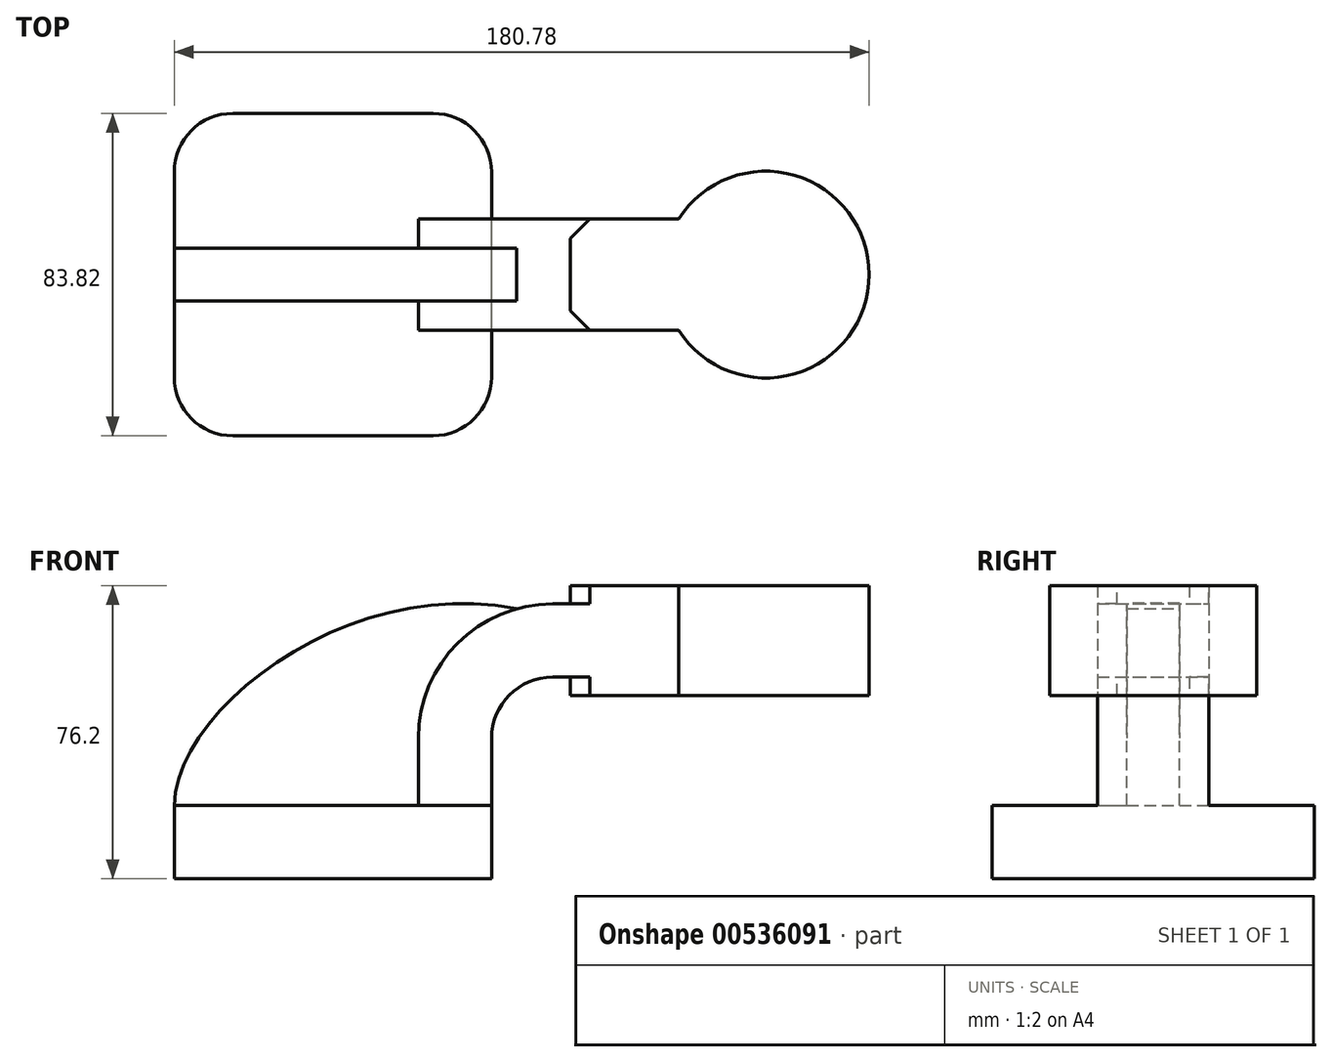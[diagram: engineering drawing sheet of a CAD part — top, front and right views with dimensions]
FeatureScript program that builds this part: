
annotation { "Feature Type Name" : "Feature", "Feature Type Description" : "" }
export const myFeature = defineFeature(function(context is Context, id is Id, definition is map)
    precondition{}
    {
        {
            var Q0;
            Q0=qCreatedBy(makeId("Front.planeOp"),FACE);
            var sketch = newSketch(context, id + "F0", { "sketchPlane" : qUnion([Q0])});
            skLineSegment(sketch, "E0.bottom", {"start": v(-41.28, 9.52) * mm, "end": v(41.27, 9.53) * mm});
            skLineSegment(sketch, "E0.top", {"start": v(-41.28, -9.53) * mm, "end": v(41.28, -9.53) * mm});
            skLineSegment(sketch, "E0.left", {"start": v(-41.28, 9.52) * mm, "end": v(-41.28, -9.53) * mm});
            skLineSegment(sketch, "E0.right", {"start": v(41.27, 9.53) * mm, "end": v(41.28, -9.52) * mm});
            skPoint(sketch, "E0.middle", {"position": v(0, 0) * mm});
            skLineSegment(sketch, "E1.bottom", {"start": v(61.81, 38.1) * mm, "end": v(112.61, 38.1) * mm});
            skLineSegment(sketch, "E1.top", {"start": v(61.81, 66.68) * mm, "end": v(112.61, 66.68) * mm});
            skLineSegment(sketch, "E1.left", {"start": v(61.81, 38.1) * mm, "end": v(61.81, 66.68) * mm});
            skLineSegment(sketch, "E1.right", {"start": v(112.61, 38.1) * mm, "end": v(112.61, 66.68) * mm});
            skPoint(sketch, "E1.middle", {"position": v(87.21, 52.39) * mm});
            skLineSegment(sketch, "E2", {"start": v(41.27, 9.53) * mm, "end": v(41.27, 27) * mm});
            skArc(sketch, "E3", {"start": v(41.27, 27) * mm, "mid": v(45.92, 38.23) * mm, "end": v(57.15, 42.88) * mm});
            skLineSegment(sketch, "E4", {"start": v(57.15, 42.88) * mm, "end": v(85.72, 42.88) * mm});
            skLineSegment(sketch, "E5.0", {"start": v(57.15, 61.93) * mm, "end": v(85.72, 61.93) * mm});
            skArc(sketch, "E5.1", {"start": v(22.22, 27) * mm, "mid": v(32.45, 51.7) * mm, "end": v(57.15, 61.93) * mm});
            skLineSegment(sketch, "E5.2", {"start": v(22.22, 9.53) * mm, "end": v(22.22, 27) * mm});
            skLineSegment(sketch, "E6", {"start": v(85.72, 42.88) * mm, "end": v(85.72, 66.68) * mm});
            skPoint(sketch, "E6.endSnap0", {"position": v(87.21, 66.68) * mm});
            skLineSegment(sketch, "E7", {"start": v(85.72, 66.68) * mm, "end": v(85.72, 38.1) * mm});
            skPoint(sketch, "E7.endSnap0", {"position": v(87.21, 38.1) * mm});
            skFitSpline(sketch, "E8", {"points": [v(-41.28, 9.53) * mm, v(47.83, 60.66) * mm], "startDerivative": vector(2.6, 78.56) * mm, "endDerivative": vector(127.58, -26.35) * mm});
            skSolve(sketch);
        }
        {
            var Q0;
            Q0=makeQuery(id+"F0.imprint","IMPRINT",FACE,{"disambiguationData":[TD([[makeQuery(id+"F0.imprint","IMPRINT",EDGE,{"derivedFrom":sQuery(id+"F0.wireOp",EDGE,"E0.top")}),1.0]])]});
            extrude(context, id + "F1", {"entities" : qUnion([Q0]), "endBound" : BoundingType.SYMMETRIC, "depth" : 83.82 * mm, "offsetDistance" : 25.4 * mm});
        }
        {
            var Q0;
            {var subQ0=sQuery(id+"F0.wireOp",EDGE,"E4");var subQ1=sQuery(id+"F0.wireOp",EDGE,"E1.left");var subQ2=makeQuery(id+"F0.imprint","INTERSECT",VERTEX,{"derivedFrom":[subQ1,subQ0]});Q0=makeQuery(id+"F0.imprint","IMPRINT",FACE,{"disambiguationData":[TD([[makeQuery(id+"F0.imprint","IMPRINT",EDGE,{"disambiguationData":[TD([[subQ2,-1.0]])],"derivedFrom":subQ1}),-1.0]])]});}
            var Q1;
            {var subQ4=sQuery(id+"F0.wireOp",EDGE,"E1.right");Q1=makeQuery(id+"F0.imprint","IMPRINT",FACE,{"disambiguationData":[TD([[makeQuery(id+"F0.imprint","IMPRINT",EDGE,{"derivedFrom":subQ4}),1.0]])]});}
            var Q2;
            {var subQ0=sQuery(id+"F0.wireOp",EDGE,"E1.left");var subQ1=sQuery(id+"F0.wireOp",EDGE,"E1.top");var subQ2=makeQuery(id+"F0.imprint","INTERSECT",VERTEX,{"derivedFrom":[subQ1,subQ0]});Q2=makeQuery(id+"F0.imprint","IMPRINT",FACE,{"disambiguationData":[TD([[makeQuery(id+"F0.imprint","IMPRINT",EDGE,{"disambiguationData":[TD([[subQ2,-1.0]])],"derivedFrom":subQ1}),-1.0]])]});}
            var Q3;
            {var subQ0=sQuery(id+"F0.wireOp",EDGE,"E1.left");var subQ1=sQuery(id+"F0.wireOp",EDGE,"E1.bottom");var subQ2=makeQuery(id+"F0.imprint","INTERSECT",VERTEX,{"derivedFrom":[subQ1,subQ0]});Q3=makeQuery(id+"F0.imprint","IMPRINT",FACE,{"disambiguationData":[TD([[makeQuery(id+"F0.imprint","IMPRINT",EDGE,{"disambiguationData":[TD([[subQ2,-1.0]])],"derivedFrom":subQ1}),1.0]])]});}
            var Q4;
            {var subQ1=sQuery(id+"F0.wireOp",EDGE,"E2");Q4=makeQuery(id+"F0.imprint","IMPRINT",FACE,{"disambiguationData":[TD([[makeQuery(id+"F0.imprint","IMPRINT",EDGE,{"derivedFrom":subQ1}),1.0]])]});}
            extrude(context, id + "F2", {"entities" : qUnion([Q0, Q1, Q2, Q3, Q4]), "operationType" : NewBodyOperationType.ADD, "endBound" : BoundingType.SYMMETRIC, "depth" : 28.96 * mm, "offsetDistance" : 25.4 * mm});
        }
        {
            var Q0;
            {var subQ2=sQuery(id+"F0.wireOp",EDGE,"E5.2");Q0=makeQuery(id+"F0.imprint","IMPRINT",FACE,{"disambiguationData":[TD([[makeQuery(id+"F0.imprint","IMPRINT",EDGE,{"derivedFrom":subQ2}),1.0]])]});}
            extrude(context, id + "F3", {"entities" : qUnion([Q0]), "operationType" : NewBodyOperationType.ADD, "endBound" : BoundingType.SYMMETRIC, "depth" : 13.72 * mm, "offsetDistance" : 25.4 * mm});
        }
        {
            var Q0;
            {var subQ4=sQuery(id+"F0.wireOp",EDGE,"E1.right");Q0=makeQuery(id+"F0.imprint","IMPRINT",FACE,{"disambiguationData":[TD([[makeQuery(id+"F0.imprint","IMPRINT",EDGE,{"derivedFrom":subQ4}),1.0]])]});}
            var Q1;
            Q1=sQuery(id+"F0.wireOp",EDGE,"E1.right");
            revolve(context, id + "F4", {"operationType" : NewBodyOperationType.ADD, "entities" : qUnion([Q0]), "axis" : qUnion([Q1]), "revolveType" : RevolveType.FULL});
        }
        {
            var Q0;
            Q0=makeQuery(id+"F1.opExtrude","CAP_EDGE",EDGE,{"disambiguationData":[OSD([sQuery(id+"F0.wireOp",EDGE,"E0.left")])],"isStart":false});
            var Q1;
            Q1=makeQuery(id+"F1.opExtrude","CAP_EDGE",EDGE,{"disambiguationData":[OSD([sQuery(id+"F0.wireOp",EDGE,"E0.right")])],"isStart":false});
            var Q2;
            Q2=makeQuery(id+"F1.opExtrude","CAP_EDGE",EDGE,{"disambiguationData":[OSD([sQuery(id+"F0.wireOp",EDGE,"E0.right")])],"isStart":true});
            var Q3;
            Q3=makeQuery(id+"F1.opExtrude","CAP_EDGE",EDGE,{"disambiguationData":[OSD([sQuery(id+"F0.wireOp",EDGE,"E0.left")])],"isStart":true});
            fillet(context, id + "F5", {"entities" : qUnion([Q0, Q1, Q2, Q3]), "radius" : 15.24 * mm, "tangentPropagation" : true, "allowEdgeOverflow" : false});
        }
        {
            var Q0;
            {var subQ0=sQuery(id+"F0.wireOp",EDGE,"E1.left");Q0=makeQuery(id+"F2.opExtrude","CAP_EDGE",EDGE,{"disambiguationData":[OSD([subQ0]),TDD([makeQuery(id+"F0.imprint","IMPRINT",EDGE,{"disambiguationData":[TD([[makeQuery(id+"F0.imprint","INTERSECT",VERTEX,{"derivedFrom":[sQuery(id+"F0.wireOp",EDGE,"E1.top"),subQ0]}),1.0]])],"derivedFrom":subQ0})])],"isStart":false});}
            var Q1;
            {var subQ0=sQuery(id+"F0.wireOp",EDGE,"E1.left");Q1=makeQuery(id+"F2.opExtrude","CAP_EDGE",EDGE,{"disambiguationData":[OSD([subQ0]),TDD([makeQuery(id+"F0.imprint","IMPRINT",EDGE,{"disambiguationData":[TD([[makeQuery(id+"F0.imprint","INTERSECT",VERTEX,{"derivedFrom":[sQuery(id+"F0.wireOp",EDGE,"E1.bottom"),subQ0]}),-1.0]])],"derivedFrom":subQ0})])],"isStart":false});}
            var Q2;
            {var subQ0=sQuery(id+"F0.wireOp",EDGE,"E1.left");Q2=makeQuery(id+"F2.opExtrude","CAP_EDGE",EDGE,{"disambiguationData":[OSD([subQ0]),TDD([makeQuery(id+"F0.imprint","IMPRINT",EDGE,{"disambiguationData":[TD([[makeQuery(id+"F0.imprint","INTERSECT",VERTEX,{"derivedFrom":[sQuery(id+"F0.wireOp",EDGE,"E1.top"),subQ0]}),1.0]])],"derivedFrom":subQ0})])],"isStart":true});}
            var Q3;
            {var subQ0=sQuery(id+"F0.wireOp",EDGE,"E1.left");Q3=makeQuery(id+"F2.opExtrude","CAP_EDGE",EDGE,{"disambiguationData":[OSD([subQ0]),TDD([makeQuery(id+"F0.imprint","IMPRINT",EDGE,{"disambiguationData":[TD([[makeQuery(id+"F0.imprint","INTERSECT",VERTEX,{"derivedFrom":[sQuery(id+"F0.wireOp",EDGE,"E1.bottom"),subQ0]}),-1.0]])],"derivedFrom":subQ0})])],"isStart":true});}
            chamfer(context, id + "F6", {"entities" : qUnion([Q0, Q1, Q2, Q3]), "width" : 5.08 * mm, "tangentPropagation" : true});
        }
    });
